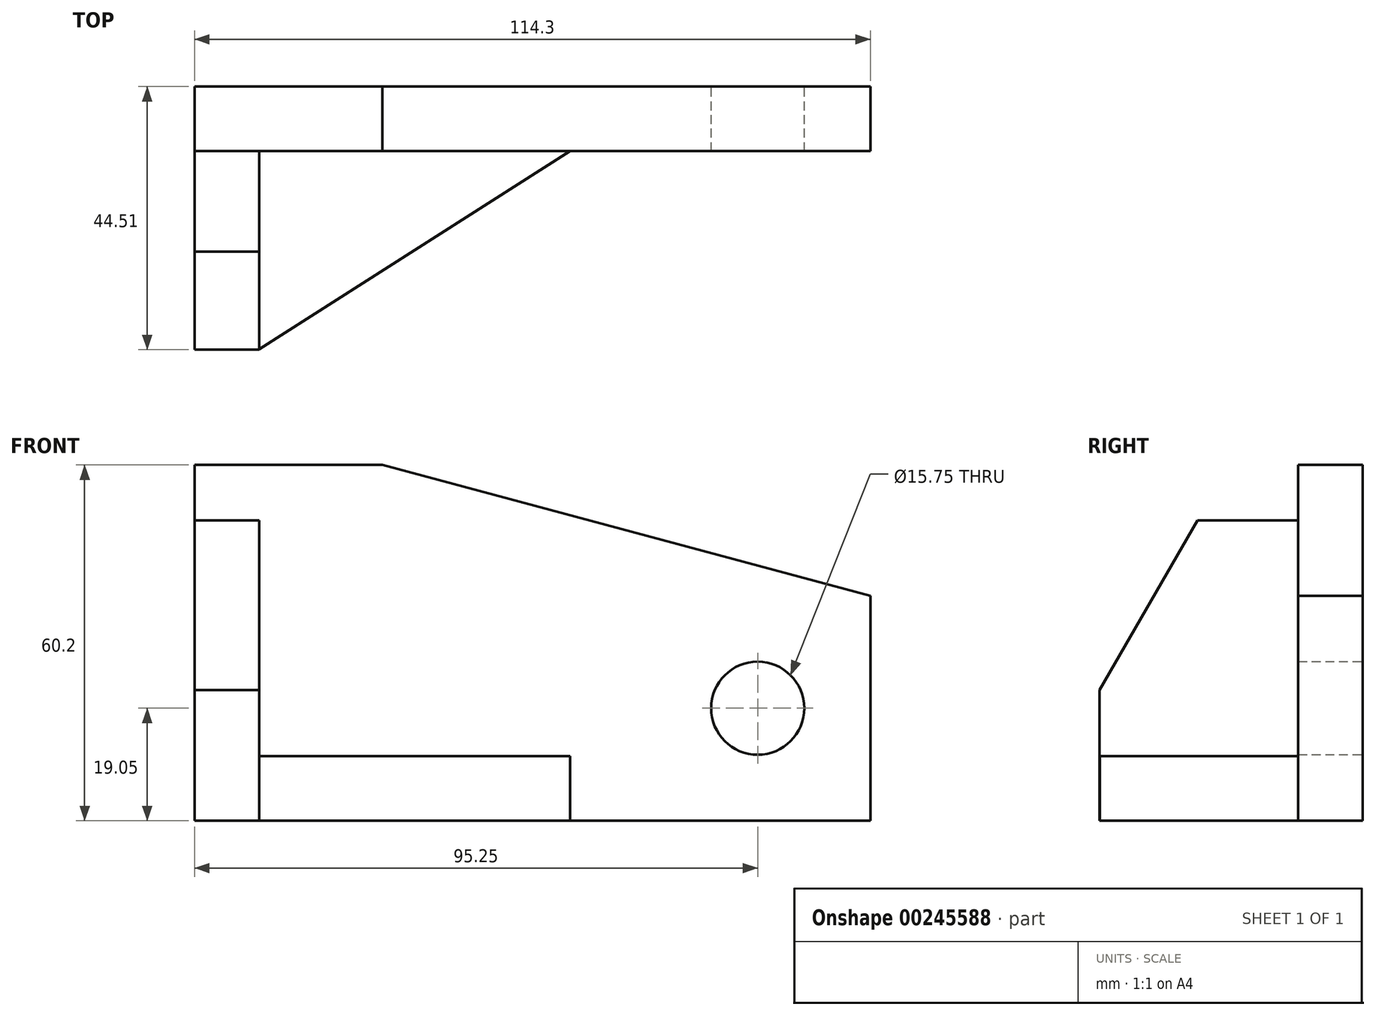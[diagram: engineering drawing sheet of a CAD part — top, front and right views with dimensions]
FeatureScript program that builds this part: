
annotation { "Feature Type Name" : "Feature", "Feature Type Description" : "" }
export const myFeature = defineFeature(function(context is Context, id is Id, definition is map)
    precondition{}
    {
        {
            var Q0;
            Q0=qCreatedBy(makeId("Front.planeOp"),FACE);
            var sketch = newSketch(context, id + "F0", { "sketchPlane" : qUnion([Q0])});
            skCircle(sketch, "E0", {"center": v(0, 0) * mm, "radius": 7.87 * mm});
            skLineSegment(sketch, "E1", {"start": v(-95.25, -19.05) * mm, "end": v(19.05, -19.05) * mm});
            skPoint(sketch, "E2", {"position": v(19.05, -19.05) * mm});
            skPoint(sketch, "E3", {"position": v(-63.5, 41.15) * mm});
            skLineSegment(sketch, "E4", {"start": v(-95.25, 41.15) * mm, "end": v(-95.25, -19.05) * mm});
            skPoint(sketch, "E5", {"position": v(-31.75, -19.05) * mm});
            skPoint(sketch, "E6", {"position": v(-84.33, -19.05) * mm});
            skPoint(sketch, "E7", {"position": v(-95.25, 31.75) * mm});
            skLineSegment(sketch, "E8", {"start": v(-63.5, 41.15) * mm, "end": v(19.05, 19.03) * mm});
            skLineSegment(sketch, "E9", {"start": v(-95.25, 41.15) * mm, "end": v(-63.5, 41.15) * mm});
            skLineSegment(sketch, "E10", {"start": v(19.05, 19.03) * mm, "end": v(19.05, -19.05) * mm});
            skLineSegment(sketch, "E11", {"start": v(-84.33, -19.05) * mm, "end": v(-84.33, 31.75) * mm});
            skLineSegment(sketch, "E12", {"start": v(-95.25, 31.75) * mm, "end": v(-84.33, 31.75) * mm});
            skPoint(sketch, "E13", {"position": v(-95.25, 3.05) * mm});
            skLineSegment(sketch, "E14", {"start": v(-31.75, -19.05) * mm, "end": v(-31.75, -8.13) * mm});
            skLineSegment(sketch, "E15", {"start": v(-31.75, -8.13) * mm, "end": v(-84.33, -8.13) * mm});
            skLineSegment(sketch, "E16", {"start": v(-63.5, 41.15) * mm, "end": v(-25.08, 41.15) * mm, "construction": true});
            skSolve(sketch);
        }
        {
            var Q0;
            Q0=makeQuery(id+"F0.imprint","IMPRINT",FACE,{"disambiguationData":[TD([[makeQuery(id+"F0.imprint","IMPRINT",EDGE,{"derivedFrom":sQuery(id+"F0.wireOp",EDGE,"E0")}),-1.0]])]});
            extrude(context, id + "F1", {"entities" : qUnion([Q0]), "depth" : 10.92 * mm});
        }
        {
            var Q0;
            Q0=makeQuery(id+"F1.opExtrude","SWEPT_FACE",FACE,{"disambiguationData":[OSD([sQuery(id+"F0.wireOp",EDGE,"E15")])]});
            var sketch = newSketch(context, id + "F2", { "sketchPlane" : qUnion([Q0])});
            skLineSegment(sketch, "E17", {"start": v(-84.33, 0) * mm, "end": v(-84.33, 44.45) * mm});
            skLineSegment(sketch, "E18", {"start": v(-84.33, 44.45) * mm, "end": v(-31.75, 10.92) * mm});
            skLineSegment(sketch, "E19", {"start": v(-31.75, 10.92) * mm, "end": v(-31.75, 0) * mm});
            skLineSegment(sketch, "E20", {"start": v(-31.75, 0) * mm, "end": v(-84.33, 0) * mm});
            skSolve(sketch);
        }
        {
            var Q0;
            Q0 = qSketchRegion(id + "F2", true);
            extrude(context, id + "F3", {"entities" : qUnion([Q0]), "operationType" : NewBodyOperationType.ADD, "depth" : 10.92 * mm});
        }
        {
            var Q0;
            Q0=makeQuery(id+"F3.boolean.opBoolean","MERGE",FACE,{"derivedFrom":[makeQuery(id+"F1.opExtrude","SWEPT_FACE",FACE,{"disambiguationData":[OSD([sQuery(id+"F0.wireOp",EDGE,"E11")])]}),makeQuery(id+"F3.opExtrude","SWEPT_FACE",FACE,{"disambiguationData":[OSD([sQuery(id+"F2.wireOp",EDGE,"E17")])]})]});
            var sketch = newSketch(context, id + "F4", { "sketchPlane" : qUnion([Q0])});
            skLineSegment(sketch, "E21", {"start": v(44.51, 3.05) * mm, "end": v(44.51, -19.05) * mm});
            skLineSegment(sketch, "E22", {"start": v(44.51, -19.05) * mm, "end": v(0, -19.05) * mm});
            skLineSegment(sketch, "E23", {"start": v(0, -19.05) * mm, "end": v(0, 31.75) * mm});
            skLineSegment(sketch, "E24", {"start": v(44.51, -8.13) * mm, "end": v(44.51, 31.75) * mm, "construction": true});
            skPoint(sketch, "E24.endSnap0", {"position": v(5.46, 31.75) * mm});
            skLineSegment(sketch, "E25", {"start": v(44.51, 3.05) * mm, "end": v(27.94, 31.75) * mm});
            skLineSegment(sketch, "E26", {"start": v(0, 31.75) * mm, "end": v(27.94, 31.75) * mm});
            skSolve(sketch);
        }
        {
            var Q0;
            Q0 = qSketchRegion(id + "F4", true);
            extrude(context, id + "F5", {"entities" : qUnion([Q0]), "operationType" : NewBodyOperationType.ADD, "depth" : 10.92 * mm});
        }
    });
